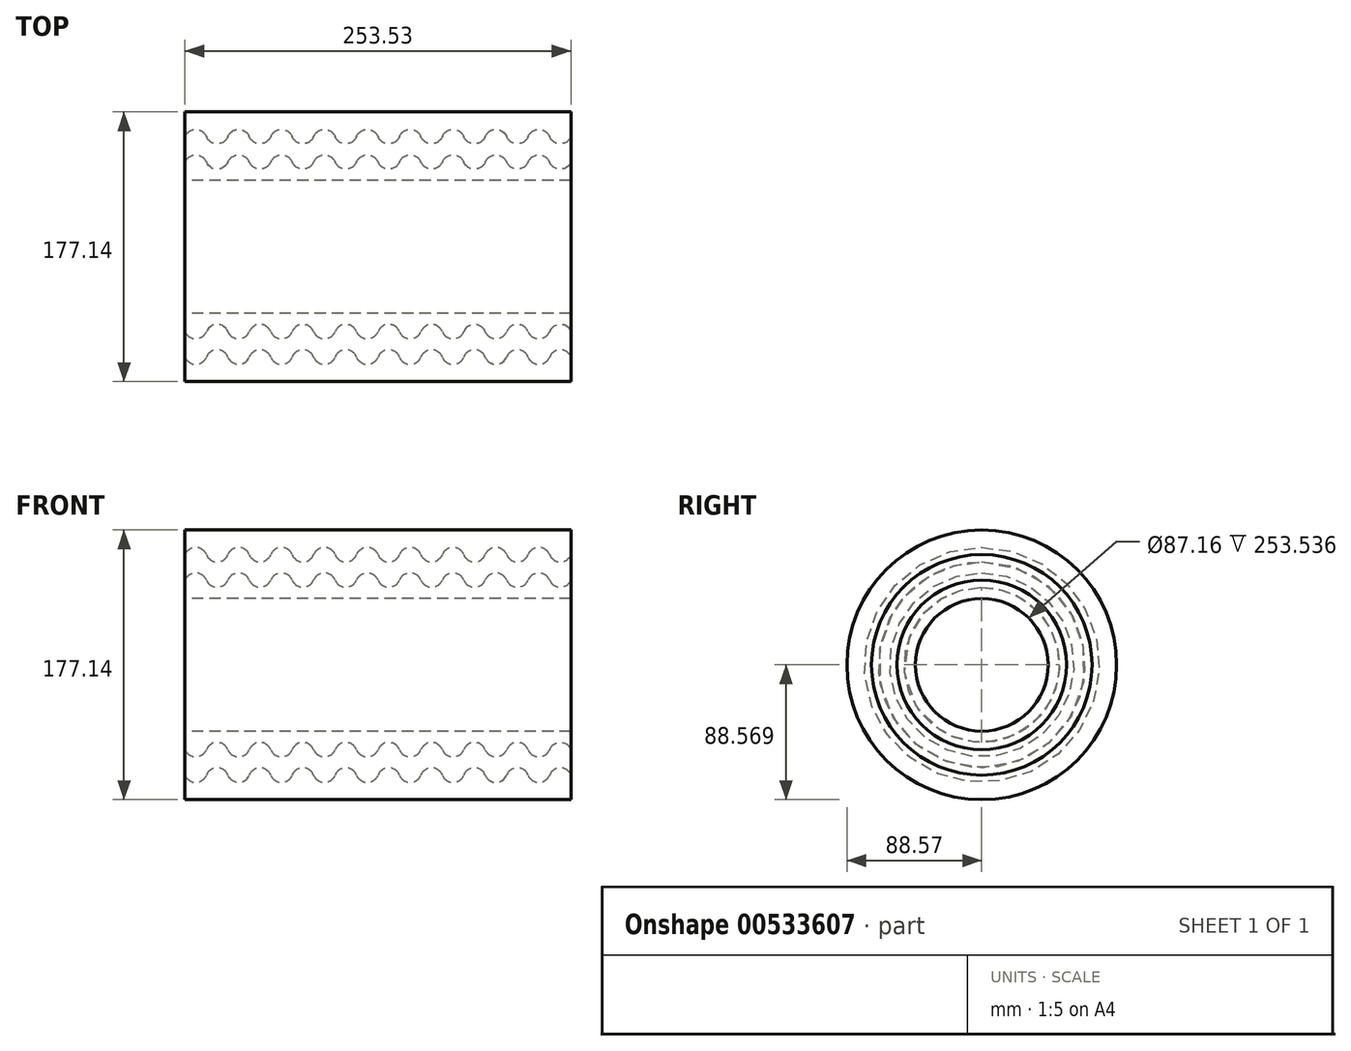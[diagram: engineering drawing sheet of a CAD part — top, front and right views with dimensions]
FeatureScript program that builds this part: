
annotation { "Feature Type Name" : "Feature", "Feature Type Description" : "" }
export const myFeature = defineFeature(function(context is Context, id is Id, definition is map)
    precondition{}
    {
        {
            var Q0;
            Q0=qCreatedBy(makeId("Front.planeOp"),FACE);
            var sketch = newSketch(context, id + "F0", { "sketchPlane" : qUnion([Q0])});
            skLineSegment(sketch, "E0.bottom", {"start": v(-106.77, 68.55) * mm, "end": v(146.76, 68.55) * mm});
            skLineSegment(sketch, "E0.top", {"start": v(-106.77, 23.56) * mm, "end": v(146.76, 23.56) * mm});
            skLineSegment(sketch, "E0.left", {"start": v(-106.77, 68.55) * mm, "end": v(-106.77, 23.56) * mm});
            skLineSegment(sketch, "E0.right", {"start": v(146.76, 68.55) * mm, "end": v(146.76, 23.56) * mm});
            skArc(sketch, "E1", {"start": v(-92.69, 35.69) * mm, "mid": v(-99.73, 40.44) * mm, "end": v(-106.77, 35.69) * mm});
            skArc(sketch, "E2", {"start": v(-92.69, 35.69) * mm, "mid": v(-85.64, 30.94) * mm, "end": v(-78.6, 35.69) * mm});
            skArc(sketch, "E3", {"start": v(-64.52, 35.69) * mm, "mid": v(-71.56, 40.44) * mm, "end": v(-78.6, 35.69) * mm});
            skArc(sketch, "E4", {"start": v(-64.52, 35.69) * mm, "mid": v(-57.47, 30.94) * mm, "end": v(-50.43, 35.69) * mm});
            skArc(sketch, "E5", {"start": v(-36.34, 35.69) * mm, "mid": v(-43.39, 40.44) * mm, "end": v(-50.43, 35.69) * mm});
            skArc(sketch, "E6", {"start": v(-36.34, 35.69) * mm, "mid": v(-29.3, 30.94) * mm, "end": v(-22.26, 35.69) * mm});
            skArc(sketch, "E7", {"start": v(-8.17, 35.69) * mm, "mid": v(-15.22, 40.44) * mm, "end": v(-22.26, 35.69) * mm});
            skArc(sketch, "E8", {"start": v(-8.17, 35.69) * mm, "mid": v(-1.13, 30.94) * mm, "end": v(5.91, 35.69) * mm});
            skArc(sketch, "E9", {"start": v(20, 35.69) * mm, "mid": v(12.95, 40.44) * mm, "end": v(5.91, 35.69) * mm});
            skArc(sketch, "E10", {"start": v(20, 35.69) * mm, "mid": v(27.04, 30.94) * mm, "end": v(34.08, 35.69) * mm});
            skArc(sketch, "E11", {"start": v(48.17, 35.69) * mm, "mid": v(41.12, 40.44) * mm, "end": v(34.08, 35.69) * mm});
            skArc(sketch, "E12", {"start": v(48.17, 35.69) * mm, "mid": v(55.21, 30.94) * mm, "end": v(62.25, 35.69) * mm});
            skArc(sketch, "E13", {"start": v(76.34, 35.69) * mm, "mid": v(69.3, 40.44) * mm, "end": v(62.25, 35.69) * mm});
            skArc(sketch, "E14", {"start": v(76.34, 35.69) * mm, "mid": v(83.38, 30.94) * mm, "end": v(90.42, 35.69) * mm});
            skArc(sketch, "E15", {"start": v(104.5, 35.69) * mm, "mid": v(97.47, 40.44) * mm, "end": v(90.42, 35.69) * mm});
            skArc(sketch, "E16", {"start": v(104.5, 35.69) * mm, "mid": v(111.55, 30.94) * mm, "end": v(118.6, 35.69) * mm});
            skArc(sketch, "E17", {"start": v(132.68, 35.69) * mm, "mid": v(125.64, 40.44) * mm, "end": v(118.6, 35.69) * mm});
            skArc(sketch, "E18", {"start": v(132.68, 35.69) * mm, "mid": v(139.72, 30.94) * mm, "end": v(146.76, 35.69) * mm});
            skArc(sketch, "E19", {"start": v(-92.69, 52.4) * mm, "mid": v(-99.73, 57.15) * mm, "end": v(-106.77, 52.4) * mm});
            skArc(sketch, "E20", {"start": v(-92.69, 52.4) * mm, "mid": v(-85.64, 47.65) * mm, "end": v(-78.6, 52.4) * mm});
            skArc(sketch, "E21", {"start": v(-64.52, 52.4) * mm, "mid": v(-71.56, 57.15) * mm, "end": v(-78.6, 52.4) * mm});
            skArc(sketch, "E22", {"start": v(-64.52, 52.4) * mm, "mid": v(-57.47, 47.65) * mm, "end": v(-50.43, 52.4) * mm});
            skArc(sketch, "E23", {"start": v(-36.34, 52.4) * mm, "mid": v(-43.39, 57.15) * mm, "end": v(-50.43, 52.4) * mm});
            skArc(sketch, "E24", {"start": v(-36.34, 52.4) * mm, "mid": v(-29.3, 47.65) * mm, "end": v(-22.26, 52.4) * mm});
            skArc(sketch, "E25", {"start": v(-8.17, 52.4) * mm, "mid": v(-15.22, 57.15) * mm, "end": v(-22.26, 52.4) * mm});
            skArc(sketch, "E26", {"start": v(-8.17, 52.4) * mm, "mid": v(-1.13, 47.65) * mm, "end": v(5.91, 52.4) * mm});
            skArc(sketch, "E27", {"start": v(20, 52.4) * mm, "mid": v(12.95, 57.15) * mm, "end": v(5.91, 52.4) * mm});
            skArc(sketch, "E28", {"start": v(20, 52.4) * mm, "mid": v(27.04, 47.65) * mm, "end": v(34.08, 52.4) * mm});
            skArc(sketch, "E29", {"start": v(48.17, 52.4) * mm, "mid": v(41.12, 57.15) * mm, "end": v(34.08, 52.4) * mm});
            skArc(sketch, "E30", {"start": v(48.17, 52.4) * mm, "mid": v(55.21, 47.65) * mm, "end": v(62.25, 52.4) * mm});
            skArc(sketch, "E31", {"start": v(76.34, 52.4) * mm, "mid": v(69.3, 57.15) * mm, "end": v(62.25, 52.4) * mm});
            skArc(sketch, "E32", {"start": v(76.34, 52.4) * mm, "mid": v(83.38, 47.65) * mm, "end": v(90.42, 52.4) * mm});
            skArc(sketch, "E33", {"start": v(104.5, 52.4) * mm, "mid": v(97.47, 57.15) * mm, "end": v(90.42, 52.4) * mm});
            skArc(sketch, "E34", {"start": v(104.5, 52.4) * mm, "mid": v(111.55, 47.65) * mm, "end": v(118.6, 52.4) * mm});
            skArc(sketch, "E35", {"start": v(132.68, 52.4) * mm, "mid": v(125.64, 57.15) * mm, "end": v(118.6, 52.4) * mm});
            skArc(sketch, "E36", {"start": v(132.68, 52.4) * mm, "mid": v(139.72, 47.65) * mm, "end": v(146.76, 52.4) * mm});
            skLineSegment(sketch, "E37", {"start": v(-162.3, -20.02) * mm, "end": v(221.87, -20.02) * mm, "construction": true});
            skSolve(sketch);
        }
        {
            var Q0;
            {var subQ3=sQuery(id+"F0.wireOp",EDGE,"E1");Q0=makeQuery(id+"F0.imprint","IMPRINT",FACE,{"disambiguationData":[TD([[makeQuery(id+"F0.imprint","IMPRINT",EDGE,{"derivedFrom":subQ3}),-1.0]])]});}
            var Q1;
            Q1=sQuery(id+"F0.wireOp",EDGE,"E37");
            revolve(context, id + "F1", {"entities" : qUnion([Q0]), "axis" : qUnion([Q1]), "revolveType" : RevolveType.FULL});
        }
        {
            var Q0;
            {var subQ0=sQuery(id+"F0.wireOp",EDGE,"E0.top");Q0=makeQuery(id+"F0.imprint","IMPRINT",FACE,{"disambiguationData":[TD([[makeQuery(id+"F0.imprint","IMPRINT",EDGE,{"derivedFrom":subQ0}),1.0]])]});}
            var Q1;
            Q1=sQuery(id+"F0.wireOp",EDGE,"E37");
            revolve(context, id + "F2", {"entities" : qUnion([Q0]), "axis" : qUnion([Q1]), "revolveType" : RevolveType.FULL});
        }
        {
            var Q0;
            {var subQ1=sQuery(id+"F0.wireOp",EDGE,"E0.bottom");Q0=makeQuery(id+"F0.imprint","IMPRINT",FACE,{"disambiguationData":[TD([[makeQuery(id+"F0.imprint","IMPRINT",EDGE,{"derivedFrom":subQ1}),-1.0]])]});}
            var Q1;
            Q1=sQuery(id+"F0.wireOp",EDGE,"E37");
            revolve(context, id + "F3", {"entities" : qUnion([Q0]), "axis" : qUnion([Q1]), "revolveType" : RevolveType.FULL});
        }
    });
